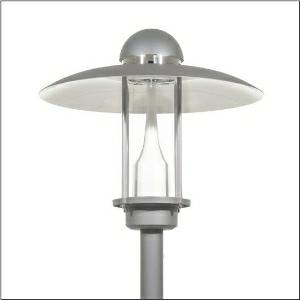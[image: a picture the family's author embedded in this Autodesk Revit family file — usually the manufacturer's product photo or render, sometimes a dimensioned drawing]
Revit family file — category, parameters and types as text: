
# Revit family: city-light_elegance_iq___p1_0a_5xa5265bf14h_371a
name_source: partatom
category: Lighting Fixtures
units: mm (PartAtom-declared; Revit-internal decimal feet)

## family parameters
Cut with Voids When Loaded = No
Host = Face
Light Source = No
Part Type = Normal
Room Calculation Point = No
Round Connector Dimension = Use Diameter
Shared = No

## types (1)
- --- (1 x LED, 1440 lm, 12.9 W, 2200K)
    Apparent Load = 13 VA
    CIE Flux Codes = 32 62 91 97 100
    Color Rendering = 70
    Color Temperature = 2200K
    Default Elevation = 1800 mm
    Description = City-Light Elegance iQ, mast luminaire, Module 540 iQ-SR, primary light control with 3 zone facetted reflector, of plastic, silver coated, highly specular, structured, primary optical cover: cover, of PMMA, transparent, light distribution: P1.0a, light emission: direct distribution, primary light characteristic: strongly asymmetric, installation type: post-top, LED, High Power LED, rated luminous flux: 1.440lm, luminous efficacy: 112lm/W, light colour: 722, colour temperature: 2200K, control gear: ECG iQ, control: presetting dimming logarithmic, Street-Remote, Auto-Match, Temp-Guard, Lumen-Switch, Night-Set, Smart-Wire, Light-Fading, Desk-Remote (wireless, voltage-free reading and setting of iQ features in the workshop via application-optimized NFC function/RFID function), optimised constant luminous flux control (CLO 2.0), with terminal, 6-pole, max. 2.5mm², mains connection: 220..240V, AC, 50/60Hz, start of lifetime: 13W, end of lifetime: 13W, reduction: 6W, luminaire housing, upper part, of aluminium, coated, Siteco® metallic grey (DB 702S), diameter: 750mm, height: 675mm, spigot size: d x l = 76 x 70mm (post-top) | with reducer (optional accessory) 60 x 70mm, post-top mast mounting element, of diecast aluminium, coated, Siteco® metallic grey (DB 702S), Module 540 iQ-SR, traffic white (RAL 9016), equipment: standard, protection rating (complete): IP65, insulation class (complete): insulation class II (safety insulation), certification: CE, ENEC, VDE, packaging unit: 1 piece

Light Distribution: P1.0a
    Height = 675 mm
    Lamp = 1 x LED
    Lamp Light Flux = 1440 lm
    Lamp Power = 12.9 W
    Lamp count = 1
    Length = 750 mm
    Luminous efficacy = 112 lm/W
    Manufacturer = Siteco
    ModVariant = No
    Model = 5XA5265BF14H
    Number of Poles = 1
    OnlyDefault = Yes
    Power Factor = 1
    Product Name = City-Light Elegance iQ | P1.0a
    Product group = mast luminaire | pylon top
    ProductGroupID = 6100
    Protection Class = Protection class II
    Protection Degree = IP 65
    RLX_Detail_Level = 1
    RlxData = <blob elided: 102133 chars, md5=d5716470>
    Socket = socket
    Standby Power = 0 W
    System Light Flux = 1440 lm
    System Power = 13 W
    Type Comments = factory setting: luminous flux: 100 % | dim-lin: 254 | 516 mA
    Type Image = l_1006912.jpg
    URL = http://relux.com
    VarID = @adj_071003
    Voltage = 0 V
    Weight = 0.00 kg
    Width = 0 mm  [stored 0 ft]

note: [stored X ft] marks values corroborated as IEEE doubles in the binary element streams (Revit-internal decimal feet)

## geometry (parser evidence)
native form markers: Blend x4, Sweep x9
no freeform markers — native parametric forms only
